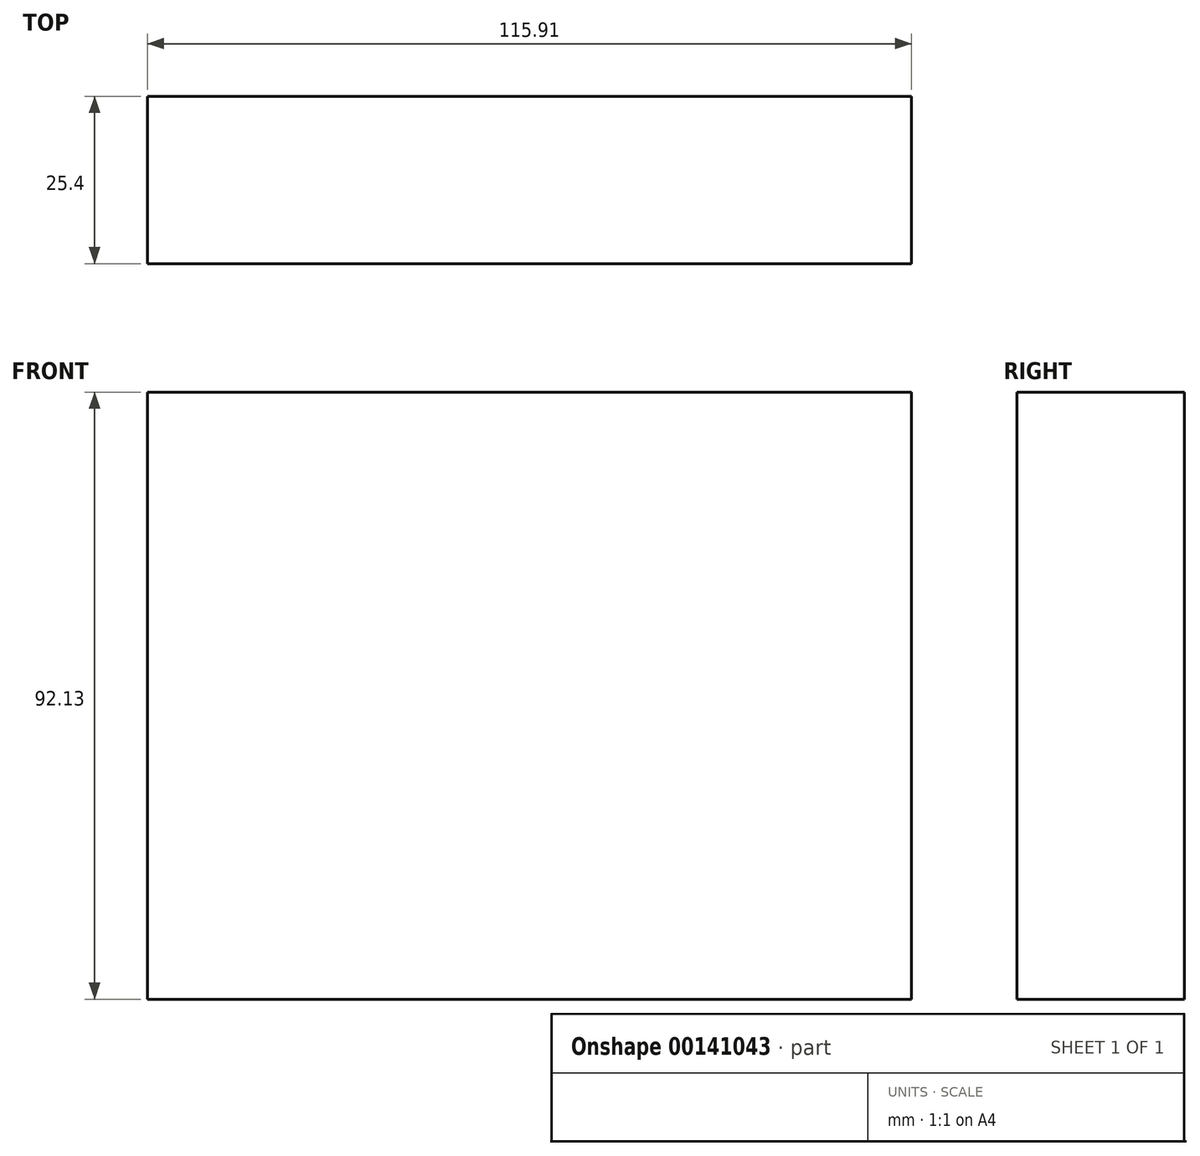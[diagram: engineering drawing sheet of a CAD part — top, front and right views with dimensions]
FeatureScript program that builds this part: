
annotation { "Feature Type Name" : "Feature", "Feature Type Description" : "" }
export const myFeature = defineFeature(function(context is Context, id is Id, definition is map)
    precondition{}
    {
        {
            var Q0;
            Q0=qCreatedBy(makeId("Front.planeOp"),FACE);
            var sketch = newSketch(context, id + "F0", { "sketchPlane" : qUnion([Q0])});
            skLineSegment(sketch, "E0.bottom", {"start": v(-65.5, 51.85) * mm, "end": v(50.4, 51.85) * mm});
            skLineSegment(sketch, "E0.top", {"start": v(-65.5, -40.28) * mm, "end": v(50.4, -40.28) * mm});
            skLineSegment(sketch, "E0.left", {"start": v(-65.5, 51.85) * mm, "end": v(-65.5, -40.28) * mm});
            skLineSegment(sketch, "E0.right", {"start": v(50.4, 51.85) * mm, "end": v(50.4, -40.28) * mm});
            skSolve(sketch);
        }
        {
            var Q0;
            Q0=makeQuery(id+"F0.imprint","IMPRINT",FACE,{"disambiguationData":[TD([[makeQuery(id+"F0.imprint","IMPRINT",EDGE,{"derivedFrom":sQuery(id+"F0.wireOp",EDGE,"E0.bottom")}),-1.0]])]});
            extrude(context, id + "F1", {"entities" : qUnion([Q0]), "depth" : 25.4 * mm});
        }
    });
